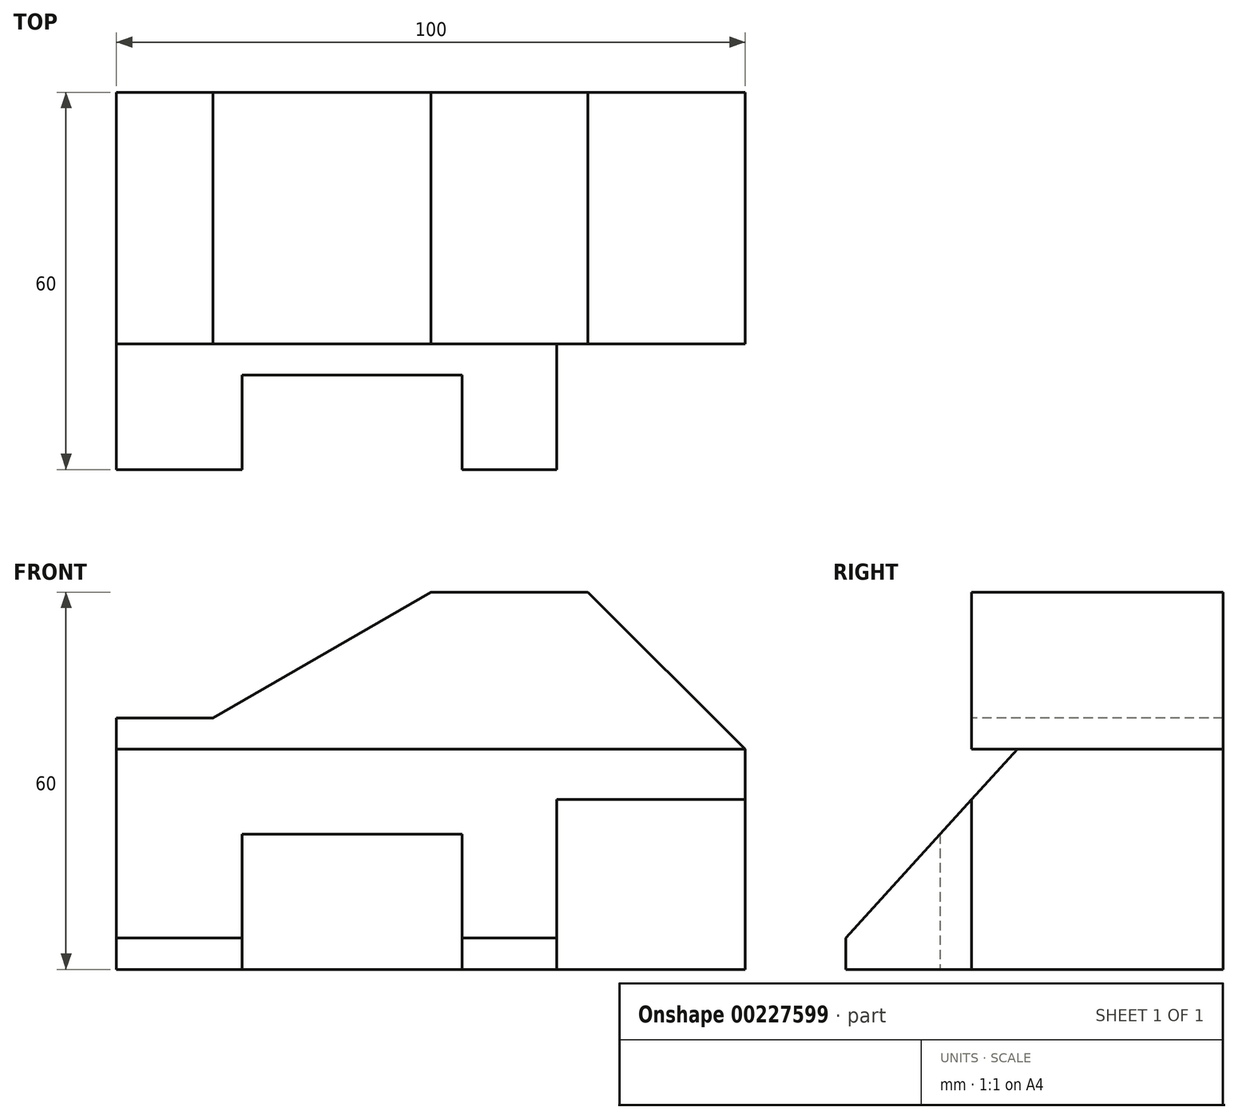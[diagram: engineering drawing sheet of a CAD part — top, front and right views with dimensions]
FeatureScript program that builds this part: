
annotation { "Feature Type Name" : "Feature", "Feature Type Description" : "" }
export const myFeature = defineFeature(function(context is Context, id is Id, definition is map)
    precondition{}
    {
        {
            var Q0;
            Q0=qCreatedBy(makeId("Top.planeOp"),FACE);
            var sketch = newSketch(context, id + "F0", { "sketchPlane" : qUnion([Q0])});
            skLineSegment(sketch, "E0", {"start": v(-84.82, 47.8) * mm, "end": v(-84.82, -12.2) * mm});
            skLineSegment(sketch, "E1", {"start": v(-84.82, -12.2) * mm, "end": v(-64.82, -12.2) * mm});
            skLineSegment(sketch, "E2", {"start": v(-64.82, -12.2) * mm, "end": v(-64.82, 2.8) * mm});
            skLineSegment(sketch, "E3", {"start": v(-64.82, 2.8) * mm, "end": v(-29.82, 2.8) * mm});
            skLineSegment(sketch, "E4", {"start": v(-29.82, 2.8) * mm, "end": v(-29.82, -12.2) * mm});
            skLineSegment(sketch, "E5", {"start": v(-29.82, -12.2) * mm, "end": v(-14.82, -12.2) * mm});
            skLineSegment(sketch, "E6", {"start": v(-14.82, -12.2) * mm, "end": v(-14.82, 7.8) * mm});
            skLineSegment(sketch, "E7", {"start": v(-14.82, 7.8) * mm, "end": v(15.18, 7.8) * mm});
            skLineSegment(sketch, "E8", {"start": v(15.18, 7.8) * mm, "end": v(15.18, 47.8) * mm});
            skLineSegment(sketch, "E9", {"start": v(15.18, 47.8) * mm, "end": v(-84.82, 47.8) * mm});
            skPoint(sketch, "E10.end.orphan", {"position": v(-74.63, 47.8) * mm});
            skPoint(sketch, "E11.start.orphan", {"position": v(-34.82, 47.8) * mm});
            skSolve(sketch);
        }
        {
            var Q0;
            Q0=makeQuery(id+"F0.imprint","IMPRINT",FACE,{"disambiguationData":[TD([[makeQuery(id+"F0.imprint","IMPRINT",EDGE,{"derivedFrom":sQuery(id+"F0.wireOp",EDGE,"E0")}),1.0]])]});
            extrude(context, id + "F1", {"entities" : qUnion([Q0]), "depth" : 60 * mm});
        }
        {
            var Q0;
            Q0=makeQuery(id+"F1.opExtrude","SWEPT_FACE",FACE,{"disambiguationData":[OSD([sQuery(id+"F0.wireOp",EDGE,"E1")])]});
            var sketch = newSketch(context, id + "F2", { "sketchPlane" : qUnion([Q0])});
            skLineSegment(sketch, "E12.0.0", {"start": v(-84.82, 0) * mm, "end": v(-64.82, 0) * mm, "construction": true});
            skLineSegment(sketch, "E12.0.1", {"start": v(-64.82, 0) * mm, "end": v(-64.82, 60) * mm, "construction": true});
            skLineSegment(sketch, "E12.0.2", {"start": v(-64.82, 60) * mm, "end": v(-84.82, 60) * mm, "construction": true});
            skLineSegment(sketch, "E12.0.3", {"start": v(-84.82, 60) * mm, "end": v(-84.82, 0) * mm, "construction": true});
            skLineSegment(sketch, "E13.0.0", {"start": v(-64.82, 0) * mm, "end": v(-29.82, 0) * mm, "construction": true});
            skLineSegment(sketch, "E13.0.1", {"start": v(-29.82, 0) * mm, "end": v(-29.82, 60) * mm, "construction": true});
            skLineSegment(sketch, "E13.0.2", {"start": v(-29.82, 60) * mm, "end": v(-64.82, 60) * mm, "construction": true});
            skLineSegment(sketch, "E13.0.3", {"start": v(-64.82, 60) * mm, "end": v(-64.82, 0) * mm, "construction": true});
            skLineSegment(sketch, "E14.0.0", {"start": v(-29.82, 0) * mm, "end": v(-14.82, 0) * mm, "construction": true});
            skLineSegment(sketch, "E14.0.1", {"start": v(-14.82, 0) * mm, "end": v(-14.82, 60) * mm, "construction": true});
            skLineSegment(sketch, "E14.0.2", {"start": v(-14.82, 60) * mm, "end": v(-29.82, 60) * mm, "construction": true});
            skLineSegment(sketch, "E14.0.3", {"start": v(-29.82, 60) * mm, "end": v(-29.82, 0) * mm, "construction": true});
            skLineSegment(sketch, "E15.0.0", {"start": v(-14.82, 0) * mm, "end": v(15.18, 0) * mm, "construction": true});
            skLineSegment(sketch, "E15.0.1", {"start": v(15.18, 0) * mm, "end": v(15.18, 60) * mm, "construction": true});
            skLineSegment(sketch, "E15.0.2", {"start": v(15.18, 60) * mm, "end": v(-14.82, 60) * mm, "construction": true});
            skLineSegment(sketch, "E15.0.3", {"start": v(-14.82, 60) * mm, "end": v(-14.82, 0) * mm, "construction": true});
            skLineSegment(sketch, "E16", {"start": v(-34.82, 60) * mm, "end": v(-69.46, 40) * mm});
            skLineSegment(sketch, "E17", {"start": v(-69.46, 40) * mm, "end": v(-84.82, 40) * mm});
            skLineSegment(sketch, "E18", {"start": v(-84.82, 40) * mm, "end": v(-84.82, 60) * mm});
            skLineSegment(sketch, "E19", {"start": v(-34.82, 60) * mm, "end": v(-84.82, 60) * mm});
            skLineSegment(sketch, "E20", {"start": v(-9.82, 60) * mm, "end": v(15.18, 35) * mm});
            skLineSegment(sketch, "E21", {"start": v(15.18, 35) * mm, "end": v(15.18, 60) * mm});
            skLineSegment(sketch, "E22", {"start": v(-9.82, 60) * mm, "end": v(15.18, 60) * mm});
            skSolve(sketch);
        }
        {
            var Q0;
            Q0 = qSketchRegion(id + "F2", true);
            extrude(context, id + "F3", {"entities" : qUnion([Q0]), "operationType" : NewBodyOperationType.REMOVE, "endBound" : BoundingType.THROUGH_ALL, "oppositeDirection" : true, "depth" : 25 * mm});
        }
        {
            var Q0;
            Q0=makeQuery(id+"F1.opExtrude","SWEPT_FACE",FACE,{"disambiguationData":[OSD([sQuery(id+"F0.wireOp",EDGE,"E6")])]});
            var sketch = newSketch(context, id + "F4", { "sketchPlane" : qUnion([Q0])});
            skLineSegment(sketch, "E23.0.0", {"start": v(-12.2, 0) * mm, "end": v(7.8, 0) * mm});
            skLineSegment(sketch, "E23.0.1", {"start": v(7.8, 0) * mm, "end": v(7.8, 60) * mm});
            skLineSegment(sketch, "E23.0.2", {"start": v(7.8, 60) * mm, "end": v(-12.2, 60) * mm});
            skLineSegment(sketch, "E23.0.3", {"start": v(-12.2, 60) * mm, "end": v(-12.2, 0) * mm});
            skLineSegment(sketch, "E24.0.0", {"start": v(47.8, 60) * mm, "end": v(7.8, 60) * mm});
            skLineSegment(sketch, "E24.0.1", {"start": v(7.8, 60) * mm, "end": v(7.8, 35) * mm});
            skLineSegment(sketch, "E24.0.2", {"start": v(7.8, 35) * mm, "end": v(47.8, 35) * mm});
            skLineSegment(sketch, "E24.0.3", {"start": v(47.8, 35) * mm, "end": v(47.8, 60) * mm});
            skLineSegment(sketch, "E25.0.0", {"start": v(47.8, 0) * mm, "end": v(47.8, 35) * mm});
            skLineSegment(sketch, "E25.0.1", {"start": v(47.8, 35) * mm, "end": v(7.8, 35) * mm});
            skLineSegment(sketch, "E25.0.2", {"start": v(7.8, 35) * mm, "end": v(7.8, 0) * mm});
            skLineSegment(sketch, "E25.0.3", {"start": v(7.8, 0) * mm, "end": v(47.8, 0) * mm});
            skLineSegment(sketch, "E26", {"start": v(37.8, 60) * mm, "end": v(-12.2, 5) * mm});
            skLineSegment(sketch, "E27", {"start": v(-12.2, 5) * mm, "end": v(-12.2, 0) * mm});
            skLineSegment(sketch, "E28", {"start": v(47.8, 0) * mm, "end": v(47.8, 60) * mm});
            skSolve(sketch);
        }
        {
            var Q0;
            Q0=makeQuery(id+"F4.imprint","IMPRINT",FACE,{"disambiguationData":[TD([[makeQuery(id+"F4.imprint","IMPRINT",EDGE,{"derivedFrom":sQuery(id+"F4.wireOp",EDGE,"E23.0.2")}),-1.0]])]});
            var Q1;
            {var subQ5=sQuery(id+"F4.wireOp",EDGE,"E24.0.1");Q1=makeQuery(id+"F4.imprint","IMPRINT",FACE,{"disambiguationData":[TD([[makeQuery(id+"F4.imprint","IMPRINT",EDGE,{"derivedFrom":subQ5}),1.0]])]});}
            var Q2;
            {var subQ1=sQuery(id+"F4.wireOp",EDGE,"E23.0.1");var subQ3=sQuery(id+"F4.wireOp",EDGE,"E26");var subQ4=makeQuery(id+"F4.imprint","INTERSECT",VERTEX,{"derivedFrom":[subQ1,subQ3]});Q2=makeQuery(id+"F4.imprint","IMPRINT",FACE,{"disambiguationData":[TD([[makeQuery(id+"F4.imprint","IMPRINT",EDGE,{"disambiguationData":[TD([[subQ4,1.0]])],"derivedFrom":subQ3}),-1.0]])]});}
            extrude(context, id + "F5", {"entities" : qUnion([Q0, Q1, Q2]), "operationType" : NewBodyOperationType.REMOVE, "endBound" : BoundingType.SYMMETRIC, "oppositeDirection" : true, "depth" : 159.4 * mm});
        }
    });
